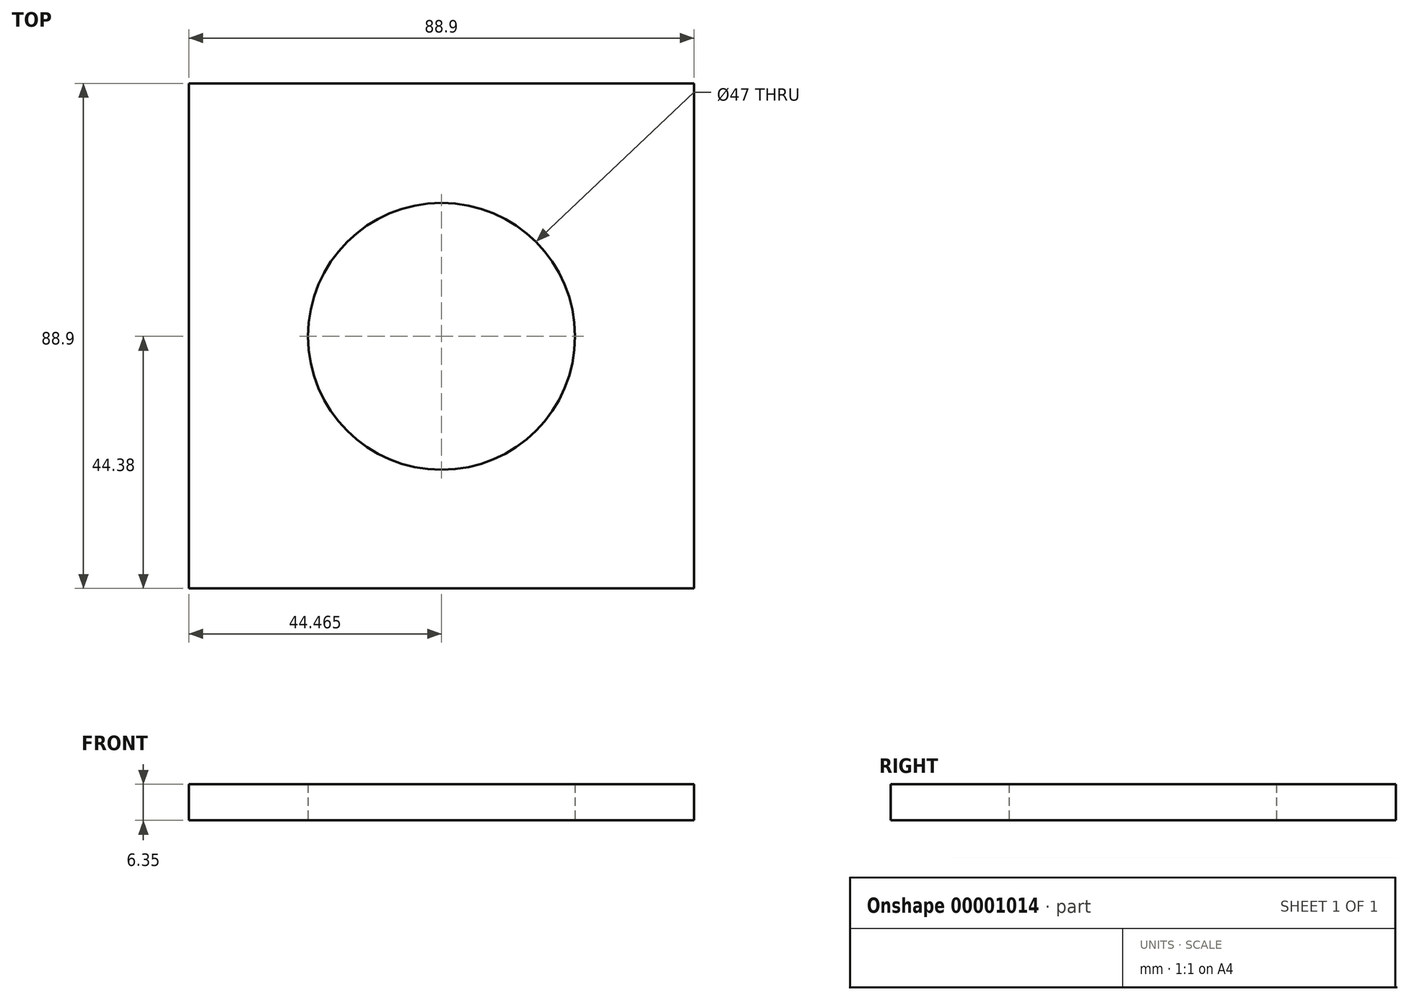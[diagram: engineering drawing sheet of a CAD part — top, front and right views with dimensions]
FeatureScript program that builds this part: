
annotation { "Feature Type Name" : "Feature", "Feature Type Description" : "" }
export const myFeature = defineFeature(function(context is Context, id is Id, definition is map)
    precondition{}
    {
        {
            var Q0;
            Q0=qCreatedBy(makeId("Top.planeOp"),FACE);
            var sketch = newSketch(context, id + "F0", { "sketchPlane" : qUnion([Q0])});
            skCircle(sketch, "E0", {"center": v(0.02, -0.07) * mm, "radius": 23.5 * mm});
            skLineSegment(sketch, "E1.rect.bottom", {"start": v(-44.45, 44.45) * mm, "end": v(44.45, 44.45) * mm});
            skLineSegment(sketch, "E1.rect.top", {"start": v(-44.45, -44.45) * mm, "end": v(44.45, -44.45) * mm});
            skLineSegment(sketch, "E1.rect.left", {"start": v(-44.45, 44.45) * mm, "end": v(-44.45, -44.45) * mm});
            skLineSegment(sketch, "E1.rect.right", {"start": v(44.45, 44.45) * mm, "end": v(44.45, -44.45) * mm});
            skPoint(sketch, "E1.rect.middle", {"position": v(0, 0) * mm});
            skSolve(sketch);
        }
        {
            var Q0;
            Q0=makeQuery(id+"F0.imprint","IMPRINT",FACE,{"disambiguationData":[TD([[makeQuery(id+"F0.imprint","IMPRINT",EDGE,{"derivedFrom":sQuery(id+"F0.wireOp",EDGE,"E0")}),-1.0]])]});
            extrude(context, id + "F1", {"entities" : qUnion([Q0]), "depth" : 6.35 * mm});
        }
    });
